# Revit family: E_Cable Tray Support_MEPcontent_OBO Bettermann_US7 FT
name_source: partatom
category: Cable Tray Fittings
revit_build: Autodesk Revit MEP 2015 (Build: 20140606_1530(x64)
units: mm (PartAtom-declared; Revit-internal decimal feet)

## types (19) — shared parameters
Article Description = Suspended support (U profile) of dimensions 70 x 50 mm with welded head plate.
Depth = 100 mm  [stored 0.328084 ft]
Description = Suspended support (U profile) of dimensions 70 x 50 mm with welded head plate.
EMCS Version = 2.0
ETIM Article Class = EC000082
Family Version = 10.14
Gray = Color RGB 189-187-185
IFCExportAs = IfcCableCarrierFittingType
IFCExportType = NOTDEFINED
MEPcontent Class = CABLE_TRAY_SUPPORT
Manufacturer = OBO BETTERMANN
Manufacturer URL = http://catalog4.obo-bettermann.com
Product Line = OBO BETTERMANN CableTrays
Revit Version = 2015
URL = www.stabiplan.com
Width 1 = 70 mm  [stored 0.229659 ft]
Width 2 = 50 mm  [stored 0.164042 ft]

## per-type parameters (varying)
| type | GTIN | Height 1 | Manufacturer Art. No. |
| US 7 K 20 FT | 4012196186556 | 200 mm  [stored 0.656168 ft] | 6339018 |
| US 7 K 30 FT | 4012196186617 | 300 mm | 6339034 |
| US 7 K 40 FT | 4012196186679 | 400 mm  [stored 1.31234 ft] | 6339050 |
| US 7 K 50 FT | 4012196186730 | 500 mm  [stored 1.64042 ft] | 6339077 |
| US 7 K 60 FT | 4012196186792 | 600 mm | 6339093 |
| US 7 K 70 FT | 4012196186853 | 700 mm  [stored 2.29659 ft] | 6339115 |
| US 7 K 80 FT | 4012196186914 | 800 mm  [stored 2.62467 ft] | 6339131 |
| US 7 K 90 FT | 4012196186976 | 900 mm  [stored 2.95276 ft] | 6339166 |
| US 7 K 100 FT | 4012196187034 | 1000 mm  [stored 3.28084 ft] | 6339182 |
| US 7 K 110 FT | 4012196187096 | 1100 mm | 6339190 |
| US 7 K 120 FT | 4012196187157 | 1200 mm | 6339204 |
| US 7 K 130 FT | 4012196187218 | 1300 mm  [stored 4.26509 ft] | 6339212 |
| US 7 K 140 FT | 4012196187270 | 1400 mm  [stored 4.59318 ft] | 6339220 |
| US 7 K 150 FT | 4012196187331 | 1500 mm  [stored 4.92126 ft] | 6339239 |
| US 7 K 160 FT | 4012196187393 | 1600 mm  [stored 5.24934 ft] | 6339247 |
| US 7 K 170 FT | 4012196187454 | 1700 mm  [stored 5.57743 ft] | 6339255 |
| US 7 K 180 FT | 4012196187515 | 1800 mm  [stored 5.90551 ft] | 6339263 |
| US 7 K 190 FT | 4012196187577 | 1900 mm  [stored 6.2336 ft] | 6339271 |
| US 7 K 200 FT | 4012196187638 | 2000 mm  [stored 6.56168 ft] | 6339298 |

note: column(s) folded — value = type name in every type: Article Type, Model

note: [stored X ft] marks values corroborated as IEEE doubles in the binary element streams (Revit-internal decimal feet)

## geometry (parser evidence)
native form markers: Blend x4, Sweep x3
no freeform markers — native parametric forms only
